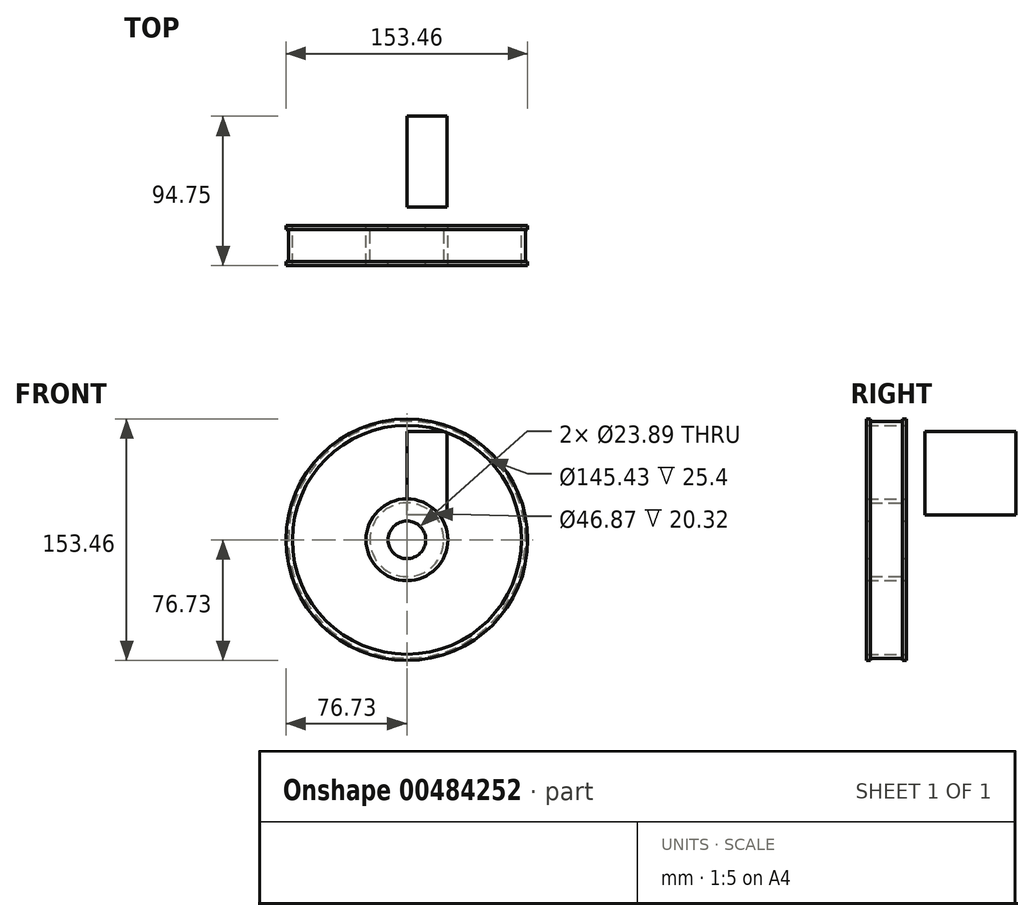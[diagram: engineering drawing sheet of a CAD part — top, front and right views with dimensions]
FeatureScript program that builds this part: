
annotation { "Feature Type Name" : "Feature", "Feature Type Description" : "" }
export const myFeature = defineFeature(function(context is Context, id is Id, definition is map)
    precondition{}
    {
        {
            var Q0;
            Q0=qCreatedBy(makeId("Front.planeOp"),FACE);
            var sketch = newSketch(context, id + "F0", { "sketchPlane" : qUnion([Q0])});
            skCircle(sketch, "E0", {"center": v(0, 0) * mm, "radius": 76.73 * mm});
            skCircle(sketch, "E1", {"center": v(0, 0) * mm, "radius": 72.72 * mm});
            skCircle(sketch, "E2", {"center": v(0, 0) * mm, "radius": 25.97 * mm});
            skCircle(sketch, "E3", {"center": v(0, 0) * mm, "radius": 11.94 * mm});
            skSolve(sketch);
        }
        {
            var Q0;
            Q0=makeQuery(id+"F0.imprint","IMPRINT",FACE,{"disambiguationData":[TD([[makeQuery(id+"F0.imprint","IMPRINT",EDGE,{"derivedFrom":sQuery(id+"F0.wireOp",EDGE,"E0")}),1.0]])]});
            var Q1;
            Q1=makeQuery(id+"F0.imprint","IMPRINT",FACE,{"disambiguationData":[TD([[makeQuery(id+"F0.imprint","IMPRINT",EDGE,{"derivedFrom":sQuery(id+"F0.wireOp",EDGE,"E2")}),1.0]])]});
            extrude(context, id + "F1", {"entities" : qUnion([Q0, Q1]), "depth" : 25.4 * mm});
        }
        {
            var Q0;
            Q0=makeQuery(id+"F1.opExtrude","SWEPT_FACE",FACE,{"disambiguationData":[OSD([sQuery(id+"F0.wireOp",EDGE,"E0")])]});
            shell(context, id + "F2", {"entities" : qUnion([Q0]), "thickness" : 2.54 * mm});
        }
        {
            var Q0;
            Q0=makeQuery(id+"F1.opExtrude","SWEPT_FACE",FACE,{"disambiguationData":[OSD([sQuery(id+"F0.wireOp",EDGE,"E3")])]});
            shell(context, id + "F3", {"entities" : qUnion([Q0]), "thickness" : 2.54 * mm});
        }
        {
            var Q0;
            Q0=qCreatedBy(makeId("Right.planeOp"),FACE);
            var sketch = newSketch(context, id + "F4", { "sketchPlane" : qUnion([Q0])});
            skLineSegment(sketch, "E4.bottom", {"start": v(70.28, 15.82) * mm, "end": v(10.76, 15.82) * mm});
            skLineSegment(sketch, "E4.top", {"start": v(70.28, 68.7) * mm, "end": v(10.76, 68.7) * mm});
            skLineSegment(sketch, "E4.left", {"start": v(70.28, 15.82) * mm, "end": v(70.28, 68.7) * mm});
            skLineSegment(sketch, "E4.right", {"start": v(10.76, 15.82) * mm, "end": v(10.76, 68.7) * mm});
            skPoint(sketch, "E4.middle", {"position": v(40.52, 42.26) * mm});
            skLineSegment(sketch, "E5.bottom", {"start": v(63, 22) * mm, "end": v(18.04, 22) * mm});
            skLineSegment(sketch, "E5.top", {"start": v(63, 62.52) * mm, "end": v(18.04, 62.52) * mm});
            skLineSegment(sketch, "E5.left", {"start": v(63, 22) * mm, "end": v(63, 62.52) * mm});
            skLineSegment(sketch, "E5.right", {"start": v(18.04, 22) * mm, "end": v(18.04, 62.52) * mm});
            skSolve(sketch);
        }
        {
            var Q0;
            Q0=qCreatedBy(makeId("Right.planeOp"),FACE);
            var sketch = newSketch(context, id + "F5", { "sketchPlane" : qUnion([Q0])});
            skLineSegment(sketch, "E6", {"start": v(41.81, 41.74) * mm, "end": v(10.93, 41.74) * mm});
            skLineSegment(sketch, "E7.0", {"start": v(69.35, 15.64) * mm, "end": v(69.35, 68.87) * mm});
            skLineSegment(sketch, "E7.1", {"start": v(11.7, 15.64) * mm, "end": v(69.35, 15.64) * mm});
            skLineSegment(sketch, "E7.2", {"start": v(11.7, 68.87) * mm, "end": v(11.7, 15.64) * mm});
            skLineSegment(sketch, "E7.3", {"start": v(69.35, 68.87) * mm, "end": v(11.7, 68.87) * mm});
            skSolve(sketch);
        }
        {
            var Q0;
            Q0=makeQuery(id+"F4.imprint","IMPRINT",FACE,{"disambiguationData":[TD([[makeQuery(id+"F4.imprint","IMPRINT",EDGE,{"derivedFrom":sQuery(id+"F4.wireOp",EDGE,"E5.bottom")}),-1.0]])]});
            var sketch = newSketch(context, id + "F6", { "sketchPlane" : qUnion([Q0])});
            skSolve(sketch);
        }
        {
            var Q0;
            Q0 = qSketchRegion(id + "F6", true);
            var Q1;
            Q1=makeQuery(id+"F5.imprint","IMPRINT",FACE,{"disambiguationData":[TD([[makeQuery(id+"F5.imprint","IMPRINT",EDGE,{"derivedFrom":sQuery(id+"F5.wireOp",EDGE,"E7.0")}),1.0]])]});
            var Q2;
            Q2=makeQuery(id+"F6.imprint","IMPRINT",FACE,{"disambiguationData":[TD([[makeQuery(id+"F6.imprint","IMPRINT",EDGE,{"derivedFrom":makeQuery(id+"F4.imprint","IMPRINT",EDGE,{"derivedFrom":sQuery(id+"F4.wireOp",EDGE,"E5.bottom")})}),-1.0]])]});
            extrude(context, id + "F7", {"entities" : qUnion([Q0, Q1, Q2]), "depth" : 25.4 * mm});
        }
    });
